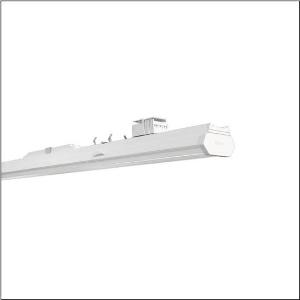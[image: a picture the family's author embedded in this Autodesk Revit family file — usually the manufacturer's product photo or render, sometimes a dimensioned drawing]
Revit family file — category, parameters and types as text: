
# Revit family: licross_r__11_protected_ho_51tp12cn4exm_ba42
name_source: partatom
category: Lighting Fixtures
units: mm (PartAtom-declared; Revit-internal decimal feet)

## family parameters
Cut with Voids When Loaded = No
Host = Face
Light Source = No
Part Type = Normal
Room Calculation Point = No
Round Connector Dimension = Use Diameter
Shared = No

## types (1)
- --- (1 x LED, 14240 lm, 77.6 W, 4000K)
    Apparent Load = 78 VA
    CIE Flux Codes = 70 91 97 98 100
    Color Rendering = 80
    Color Temperature = 4000K
    Default Elevation = 1800 mm
    Description = Licross® 11 Protected HO, luminaire insert, of sheet steel, galvanised, coil coated, white, length: 1.500mm, width: 90mm, height: 101mm, LED rated luminous flux: 14.240lm, light colour: 840, control gear: ON/OFF Multilumen, CLOi, with plug, 3-pole, with phase selection, mains connection: 220..240V, AC, 50/60Hz, start of lifetime: 78W, end of service life: 87W, halogen-free wiring, primary light control with lens, of plastic, primary optical cover: cover, of PMMA, light emission: direct distribution, primary light characteristic: symmetric, protection rating (complete): IP64, insulation class (complete): insulation class I (protective earthing), certification: CE, ENEC, VDE, UKCA, protection symbol: D if used in an environment with conductive dust loads with corresponding accessories, impact resistance: IK06, permissible ambient temperature for indoor applications: -35..+35°C, corresponds to IFS (International Featured Standards) requirements for safety and quality in the food industry, reducing of maximum allowable ambient temperature of 5°C with ceiling mounting, LABS conformity tested according to VDMA 24364:2018-05, packaging unit: 1 piece
    Height = 92 mm
    Lamp = 1 x LED
    Lamp Light Flux = 14240 lm
    Lamp Power = 77.6 W
    Lamp count = 1
    Length = 1500 mm
    Luminous efficacy = 184 lm/W
    Manufacturer = Siteco
    ModVariant = No
    Model = 51TP12CN4EXM
    Mounting Place = Ceiling
    Mounting Type = Pendant
    Number of Poles = 1
    OnlyDefault = Yes
    Power Factor = 1
    Product Name = Licross® 11 Protected HO
    Product group = luminaire insert
    ProductGroupID = 901
    Protection Class = Protection class I
    Protection Degree = IP 64
    RLX_Detail_Level = 1
    RLX_Emergency_Light_Flux = 0 lm
    RLX_Emergency_Type = 0
    RLX_Emergency_Type_DB = No
    RlxData = <blob elided: 22253 chars, md5=748025bf>
    Socket = socket
    Standby Power = 0 W
    System Light Flux = 14240 lm
    System Power = 78 W
    Type Comments = factory setting: luminous flux: 100 % | (A | C | E) | 181 mA
    Type Image = l_1256148.jpg
    URL = http://relux.com
    VarID = @adj_038141
    Voltage = 0 V
    Weight = 0.00 kg
    Width = 88 mm

## geometry (parser evidence)
native form markers: Blend x4, Sweep x11
no freeform markers — native parametric forms only
